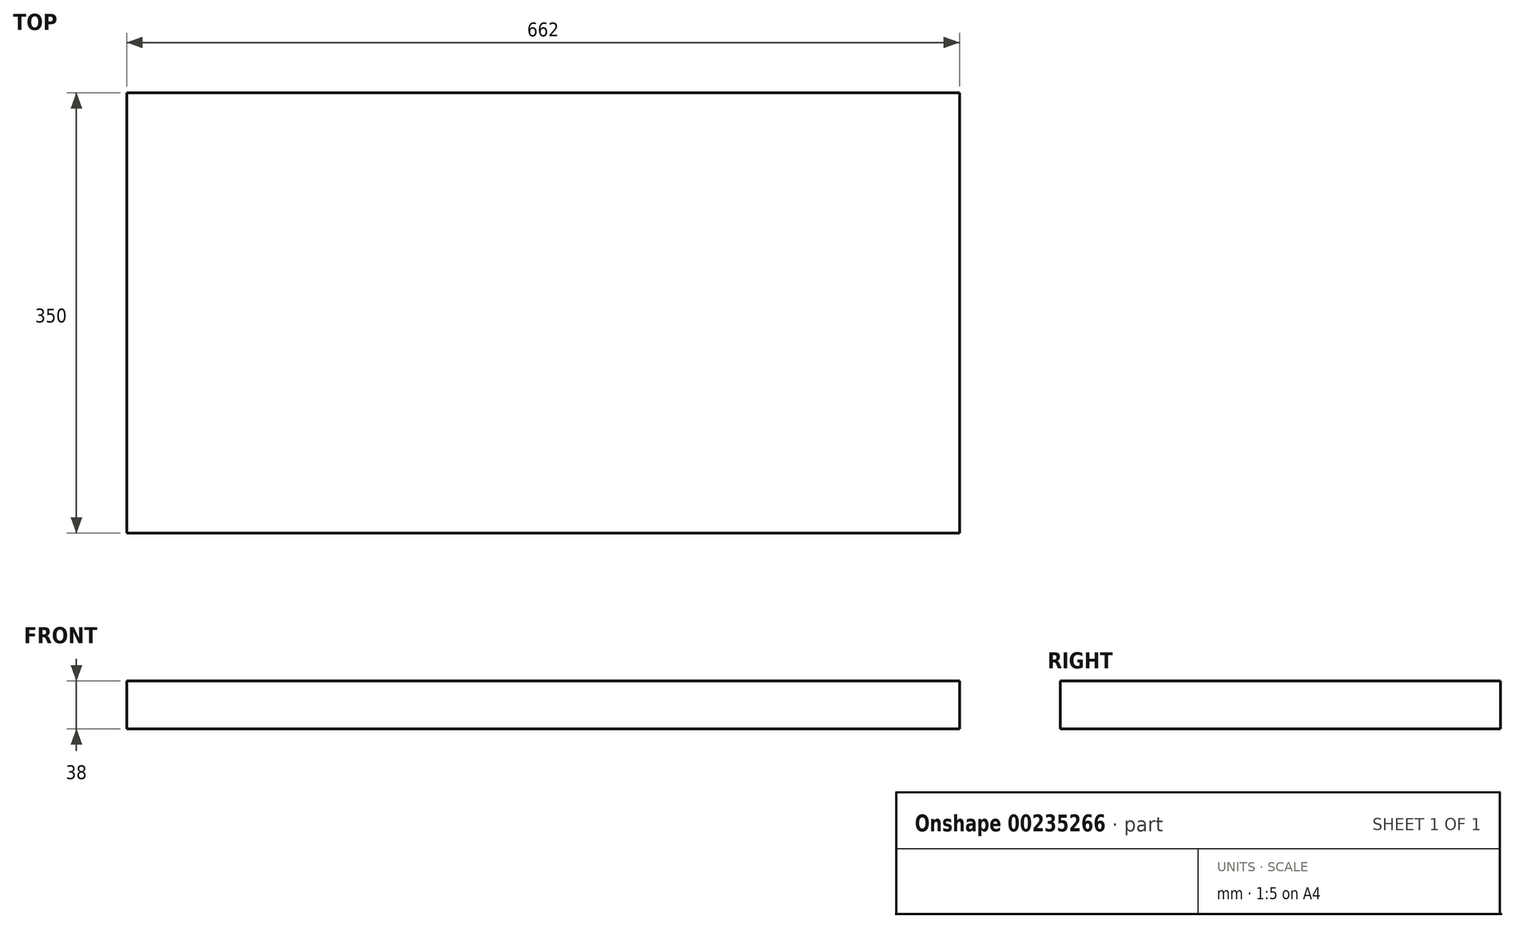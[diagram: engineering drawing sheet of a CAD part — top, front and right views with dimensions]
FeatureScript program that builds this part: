
annotation { "Feature Type Name" : "Feature", "Feature Type Description" : "" }
export const myFeature = defineFeature(function(context is Context, id is Id, definition is map)
    precondition{}
    {
        {
            var Q0;
            Q0=qCreatedBy(makeId("Right.planeOp"),FACE);
            var sketch = newSketch(context, id + "F0", { "sketchPlane" : qUnion([Q0])});
            skLineSegment(sketch, "E0.bottom", {"start": v(-263.48, 18) * mm, "end": v(86.52, 18) * mm});
            skLineSegment(sketch, "E0.top", {"start": v(-263.48, -20) * mm, "end": v(86.52, -20) * mm});
            skLineSegment(sketch, "E0.left", {"start": v(-263.48, 18) * mm, "end": v(-263.48, -20) * mm});
            skLineSegment(sketch, "E0.right", {"start": v(86.52, 18) * mm, "end": v(86.52, -20) * mm});
            skSolve(sketch);
        }
        {
            var Q0;
            Q0=makeQuery(id+"F0.imprint","IMPRINT",FACE,{"disambiguationData":[TD([[makeQuery(id+"F0.imprint","IMPRINT",EDGE,{"derivedFrom":sQuery(id+"F0.wireOp",EDGE,"E0.bottom")}),-1.0]])]});
            extrude(context, id + "F1", {"entities" : qUnion([Q0]), "depth" : 662 * mm});
        }
    });
